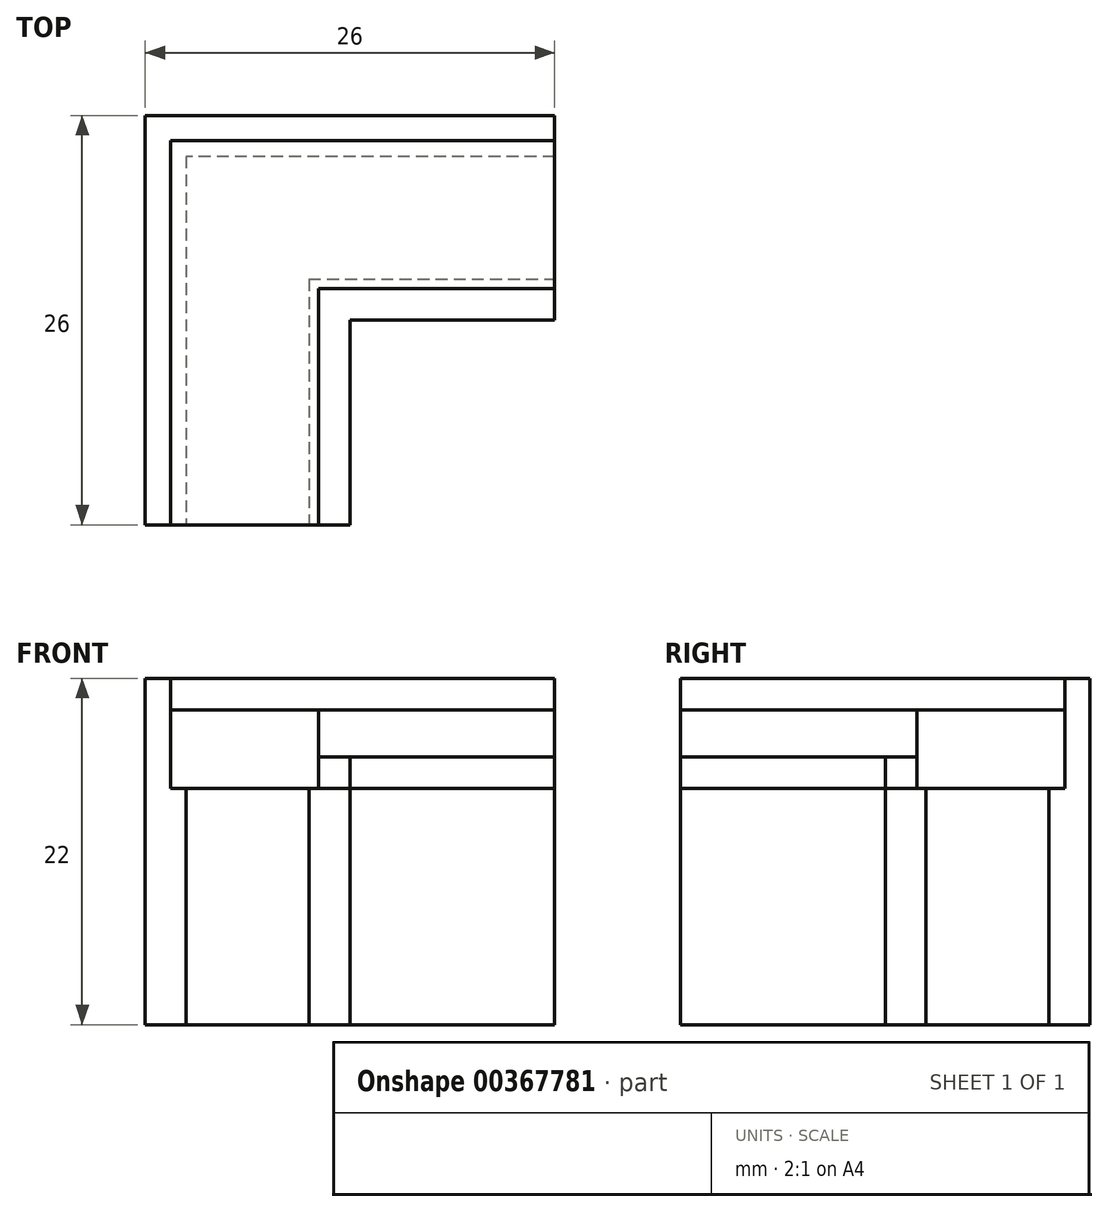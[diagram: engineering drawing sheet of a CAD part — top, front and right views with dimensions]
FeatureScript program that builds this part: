
annotation { "Feature Type Name" : "Feature", "Feature Type Description" : "" }
export const myFeature = defineFeature(function(context is Context, id is Id, definition is map)
    precondition{}
    {
        {
            var Q0;
            Q0=qCreatedBy(makeId("Top.planeOp"),FACE);
            var sketch = newSketch(context, id + "F0", { "sketchPlane" : qUnion([Q0])});
            skLineSegment(sketch, "E0.top", {"start": v(0, -13) * mm, "end": v(-13, -13) * mm});
            skLineSegment(sketch, "E0.left", {"start": v(0, 0) * mm, "end": v(0, -13) * mm});
            skLineSegment(sketch, "E0.right", {"start": v(-13, 0) * mm, "end": v(-13, -13) * mm});
            skLineSegment(sketch, "E1.bottom", {"start": v(0, 0) * mm, "end": v(13, 0) * mm});
            skLineSegment(sketch, "E1.top", {"start": v(0, 13) * mm, "end": v(13, 13) * mm});
            skLineSegment(sketch, "E1.right", {"start": v(13, 0) * mm, "end": v(13, 13) * mm});
            skLineSegment(sketch, "E2.top", {"start": v(0, 13) * mm, "end": v(-13, 13) * mm});
            skLineSegment(sketch, "E2.right", {"start": v(-13, 0) * mm, "end": v(-13, 13) * mm});
            skLineSegment(sketch, "E3.0", {"start": v(-2, 2) * mm, "end": v(-2, -13) * mm});
            skLineSegment(sketch, "E3.1", {"start": v(-2, 2) * mm, "end": v(13, 2) * mm});
            skLineSegment(sketch, "E4.0", {"start": v(-11.4, 0) * mm, "end": v(-11.4, -13) * mm});
            skLineSegment(sketch, "E4.1", {"start": v(-11.4, 0) * mm, "end": v(-11.4, 11.4) * mm});
            skLineSegment(sketch, "E4.2", {"start": v(0, 11.4) * mm, "end": v(-11.4, 11.4) * mm});
            skLineSegment(sketch, "E4.3", {"start": v(0, 11.4) * mm, "end": v(13, 11.4) * mm});
            skLineSegment(sketch, "E5.0", {"start": v(-10.4, 0) * mm, "end": v(-10.4, -13) * mm});
            skLineSegment(sketch, "E5.1", {"start": v(-10.4, 0) * mm, "end": v(-10.4, 10.4) * mm});
            skLineSegment(sketch, "E5.2", {"start": v(0, 10.4) * mm, "end": v(-10.4, 10.4) * mm});
            skLineSegment(sketch, "E5.3", {"start": v(0, 10.4) * mm, "end": v(13, 10.4) * mm});
            skLineSegment(sketch, "E6.0", {"start": v(-2.6, 2.6) * mm, "end": v(-2.6, -13) * mm});
            skLineSegment(sketch, "E6.1", {"start": v(-2.6, 2.6) * mm, "end": v(13, 2.6) * mm});
            skSolve(sketch);
        }
        {
            var Q0;
            {var subQ3=sQuery(id+"F0.wireOp",EDGE,"E4.0");Q0=makeQuery(id+"F0.imprint","IMPRINT",FACE,{"disambiguationData":[TD([[makeQuery(id+"F0.imprint","IMPRINT",EDGE,{"derivedFrom":subQ3}),1.0]])]});}
            var Q1;
            {var subQ3=sQuery(id+"F0.wireOp",EDGE,"E0.right");Q1=makeQuery(id+"F0.imprint","IMPRINT",FACE,{"disambiguationData":[TD([[makeQuery(id+"F0.imprint","IMPRINT",EDGE,{"derivedFrom":subQ3}),1.0]])]});}
            var Q2;
            {var subQ3=sQuery(id+"F0.wireOp",EDGE,"E3.0");Q2=makeQuery(id+"F0.imprint","IMPRINT",FACE,{"disambiguationData":[TD([[makeQuery(id+"F0.imprint","IMPRINT",EDGE,{"derivedFrom":subQ3}),-1.0]])]});}
            var Q3;
            {var subQ3=sQuery(id+"F0.wireOp",EDGE,"E0.left");Q3=makeQuery(id+"F0.imprint","IMPRINT",FACE,{"disambiguationData":[TD([[makeQuery(id+"F0.imprint","IMPRINT",EDGE,{"derivedFrom":subQ3}),-1.0]])]});}
            extrude(context, id + "F1", {"entities" : qUnion([Q0, Q1, Q2, Q3]), "offsetDistance" : 25 * mm, "depth" : -15 * mm});
        }
        {
            var Q0;
            {var subQ3=sQuery(id+"F0.wireOp",EDGE,"E0.right");Q0=makeQuery(id+"F0.imprint","IMPRINT",FACE,{"disambiguationData":[TD([[makeQuery(id+"F0.imprint","IMPRINT",EDGE,{"derivedFrom":subQ3}),1.0]])]});}
            extrude(context, id + "F2", {"entities" : qUnion([Q0]), "operationType" : NewBodyOperationType.ADD, "offsetDistance" : 25 * mm, "depth" : 7 * mm});
        }
        {
            var Q0;
            {var subQ3=sQuery(id+"F0.wireOp",EDGE,"E4.0");Q0=makeQuery(id+"F0.imprint","IMPRINT",FACE,{"disambiguationData":[TD([[makeQuery(id+"F0.imprint","IMPRINT",EDGE,{"derivedFrom":subQ3}),1.0]])]});}
            var Q1;
            {var subQ3=sQuery(id+"F0.wireOp",EDGE,"E5.0");Q1=makeQuery(id+"F0.imprint","IMPRINT",FACE,{"disambiguationData":[TD([[makeQuery(id+"F0.imprint","IMPRINT",EDGE,{"derivedFrom":subQ3}),1.0]])]});}
            var Q2;
            {var subQ3=sQuery(id+"F0.wireOp",EDGE,"E3.0");Q2=makeQuery(id+"F0.imprint","IMPRINT",FACE,{"disambiguationData":[TD([[makeQuery(id+"F0.imprint","IMPRINT",EDGE,{"derivedFrom":subQ3}),-1.0]])]});}
            extrude(context, id + "F3", {"entities" : qUnion([Q0, Q1, Q2]), "offsetDistance" : 25 * mm, "depth" : 5 * mm});
        }
        {
            var Q0;
            {var subQ3=sQuery(id+"F0.wireOp",EDGE,"E0.left");Q0=makeQuery(id+"F0.imprint","IMPRINT",FACE,{"disambiguationData":[TD([[makeQuery(id+"F0.imprint","IMPRINT",EDGE,{"derivedFrom":subQ3}),-1.0]])]});}
            extrude(context, id + "F4", {"entities" : qUnion([Q0]), "offsetDistance" : 25 * mm, "depth" : 2 * mm});
        }
    });
